# Revit family: Shower-Deck_Mount-Handshower-KOHLER-AVID-K-97364T_1
name_source: partatom
category: Plumbing Fixtures
revit_build: Autodesk Revit 2017 (Build: 20160225_1515(x64)
units: mm (PartAtom-declared; Revit-internal decimal feet)

## family parameters
Cut with Voids When Loaded = No
Host = Face
OmniClass Number = 23.31.17.00
OmniClass Title = Showers
Part Type = Normal
Room Calculation Point = No
Round Connector Dimension = Use Diameter
Shared = No

## types (3) — shared parameters
ADA Compliant = No
Assembly Code = D2010700
CW Connection = Yes
Cold Water Inlet = Cold Water Inlet
Date Modified = 03/03/2021
Default Elevation = 36"
Description = DIVERTER AND HANDSHOWER
Drain Included = No
Flow Rate = 3 GPM
HW Connection = Yes
Height = 9 7/16"
Hot Water Inlet = Hot Water Inlet
Length = 2 9/16"
Manufacturer = KOHLER Co.
Master Format 2014 = 22 42 23
Master Format 2014 Name = Residential Showers
Material = Brass Construction
Pressure = 80.00 psi
Product Name = AVID
URL = http://www.kohler.com.cn
Vent Connection = No
Waste Connection = No
Waste Water Outlet = Waste Water Outlet
WaterSense Certified = No

## per-type parameters (varying)
| type | Finish | Model | Type |
| CP-Polished Chrome | Kohler-Metal-CP-Polished_Chrome | K-97364T-B9-CP | 1 |
| RGD-Rose Gold | Kohler-Metal-RGD-Rose_Gold | K-97364T-B9-RGD | 2 |
| TT-Titanium Silver | Kohler-Metal-TT-Titanium_Silver | K-97364T-B9-TT | 3 |

## geometry (parser evidence)
native form markers: Sweep x6
no freeform markers — native parametric forms only
